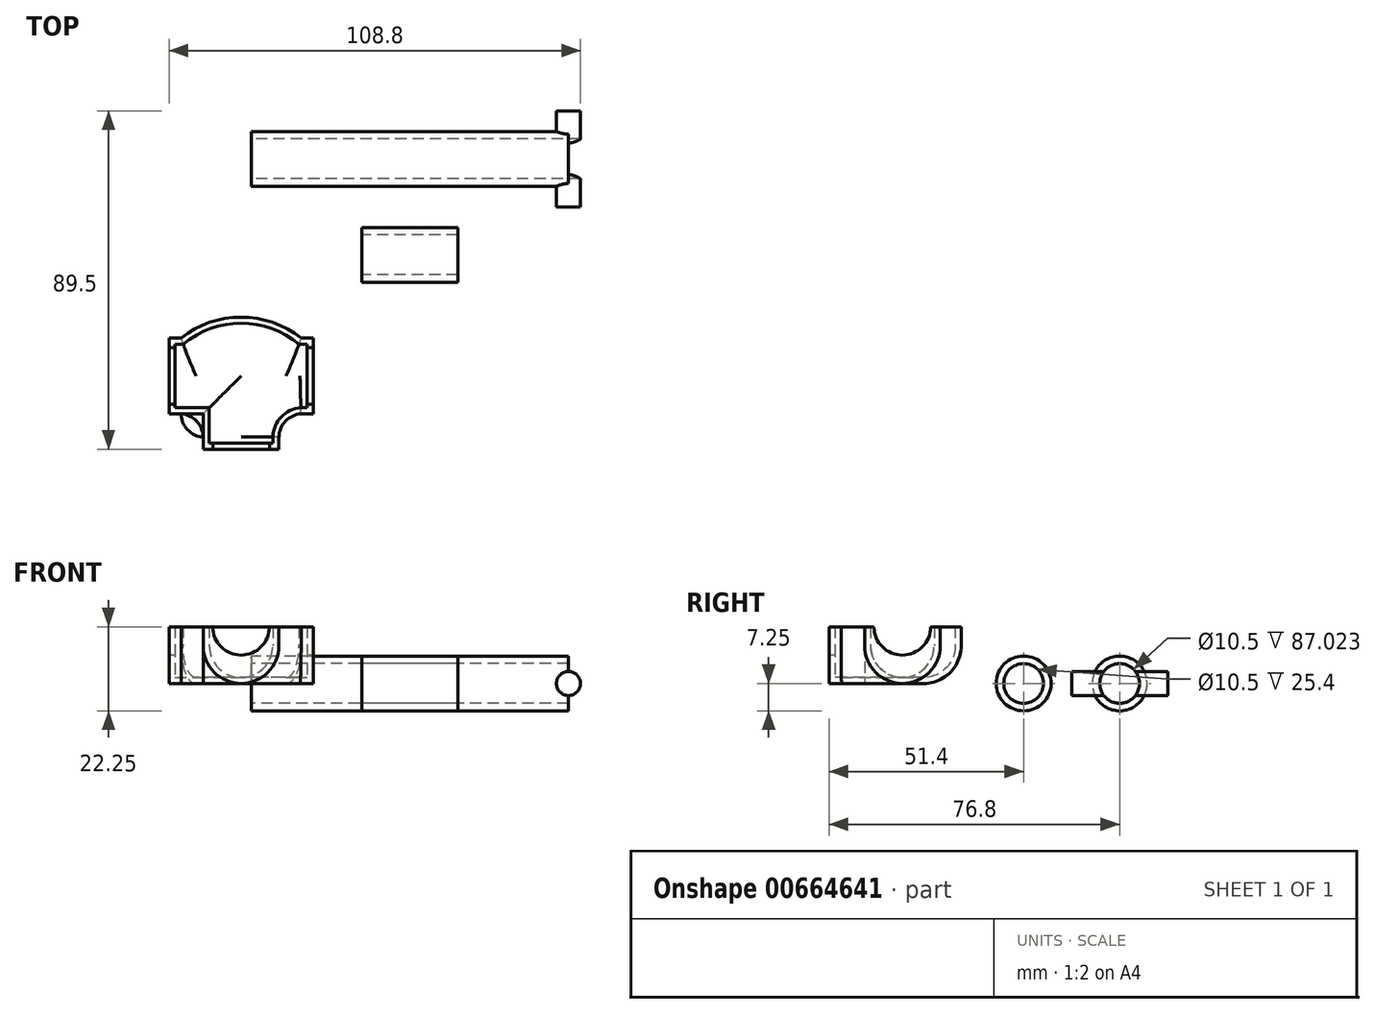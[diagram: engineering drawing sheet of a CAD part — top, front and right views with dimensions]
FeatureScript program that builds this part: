
annotation { "Feature Type Name" : "Feature", "Feature Type Description" : "" }
export const myFeature = defineFeature(function(context is Context, id is Id, definition is map)
    precondition{}
    {
        {
            var Q0;
            Q0=qCreatedBy(makeId("Right.planeOp"),FACE);
            var sketch = newSketch(context, id + "F0", { "sketchPlane" : qUnion([Q0])});
            skCircle(sketch, "E0", {"center": v(0, 0) * mm, "radius": 5.25 * mm});
            skCircle(sketch, "E1", {"center": v(0, 0) * mm, "radius": 7.25 * mm});
            skCircle(sketch, "E2.1.0.0", {"center": v(25.4, 0) * mm, "radius": 7.25 * mm});
            skCircle(sketch, "E2.1.0.1", {"center": v(25.4, 0) * mm, "radius": 5.25 * mm});
            skLineSegment(sketch, "E2.direction1", {"start": v(0, 0) * mm, "end": v(25.4, 0) * mm, "construction": true});
            skSolve(sketch);
        }
        {
            var Q0;
            Q0=makeQuery(id+"F0.imprint","IMPRINT",FACE,{"disambiguationData":[TD([[makeQuery(id+"F0.imprint","IMPRINT",EDGE,{"derivedFrom":sQuery(id+"F0.wireOp",EDGE,"E0")}),-1.0]])]});
            extrude(context, id + "F1", {"entities" : qUnion([Q0]), "endBound" : BoundingType.SYMMETRIC, "depth" : 25.4 * mm, "offsetDistance" : 25 * mm});
        }
        {
            var Q0;
            Q0=makeQuery(id+"F0.imprint","IMPRINT",FACE,{"disambiguationData":[TD([[makeQuery(id+"F0.imprint","IMPRINT",EDGE,{"derivedFrom":sQuery(id+"F0.wireOp",EDGE,"E2.1.0.0")}),1.0]])]});
            extrude(context, id + "F2", {"entities" : qUnion([Q0]), "endBound" : BoundingType.SYMMETRIC, "depth" : 83.85 * mm, "offsetDistance" : 25.4 * mm});
        }
        {
            var Q0;
            Q0=qCreatedBy(makeId("Top.planeOp"),FACE);
            var sketch = newSketch(context, id + "F3", { "sketchPlane" : qUnion([Q0])});
            skArc(sketch, "E3", {"start": v(-28.77, -22.05) * mm, "mid": v(-44.65, -16.48) * mm, "end": v(-60.52, -22.05) * mm});
            skLineSegment(sketch, "E4.bottom", {"start": v(-60.52, -22.05) * mm, "end": v(-63.7, -22.05) * mm});
            skLineSegment(sketch, "E4.top", {"start": v(-60.52, -42.05) * mm, "end": v(-63.7, -42.05) * mm});
            skLineSegment(sketch, "E4.left", {"start": v(-60.52, -22.05) * mm, "end": v(-60.52, -42.05) * mm});
            skLineSegment(sketch, "E4.right", {"start": v(-63.7, -22.05) * mm, "end": v(-63.7, -42.05) * mm});
            skLineSegment(sketch, "E5.bottom", {"start": v(-28.77, -22.05) * mm, "end": v(-25.6, -22.05) * mm});
            skLineSegment(sketch, "E5.top", {"start": v(-28.77, -42.05) * mm, "end": v(-25.6, -42.05) * mm});
            skLineSegment(sketch, "E5.left", {"start": v(-28.77, -22.05) * mm, "end": v(-28.77, -42.05) * mm});
            skLineSegment(sketch, "E5.right", {"start": v(-25.6, -22.05) * mm, "end": v(-25.6, -42.05) * mm});
            skLineSegment(sketch, "E6.bottom", {"start": v(-54.65, -48.23) * mm, "end": v(-34.65, -48.23) * mm});
            skLineSegment(sketch, "E6.top", {"start": v(-54.65, -51.4) * mm, "end": v(-34.65, -51.4) * mm});
            skLineSegment(sketch, "E6.left", {"start": v(-54.65, -48.23) * mm, "end": v(-54.65, -51.4) * mm});
            skLineSegment(sketch, "E6.right", {"start": v(-34.65, -48.23) * mm, "end": v(-34.65, -51.4) * mm});
            skArc(sketch, "E7", {"start": v(-54.65, -48.23) * mm, "mid": v(-58.78, -46.27) * mm, "end": v(-60.52, -42.05) * mm});
            skArc(sketch, "E8", {"start": v(-28.77, -42.05) * mm, "mid": v(-32.9, -44) * mm, "end": v(-34.65, -48.23) * mm});
            skLineSegment(sketch, "E9", {"start": v(-44.65, -16.48) * mm, "end": v(-44.65, -48.23) * mm});
            skArc(sketch, "E10.MirrorCS", {"start": v(-60.52, -42.05) * mm, "mid": v(-56.4, -44) * mm, "end": v(-54.65, -48.23) * mm});
            skArc(sketch, "E11.MirrorCS", {"start": v(-34.65, -48.23) * mm, "mid": v(-30.52, -46.27) * mm, "end": v(-28.77, -42.05) * mm});
            skLineSegment(sketch, "E12.bottom", {"start": v(-60.52, -22.05) * mm, "end": v(-28.77, -22.05) * mm});
            skLineSegment(sketch, "E12.top", {"start": v(-60.52, -12.53) * mm, "end": v(-28.77, -12.53) * mm});
            skLineSegment(sketch, "E12.left", {"start": v(-60.52, -22.05) * mm, "end": v(-60.52, -12.53) * mm});
            skLineSegment(sketch, "E12.right", {"start": v(-28.77, -22.05) * mm, "end": v(-28.77, -12.53) * mm});
            skArc(sketch, "E13", {"start": v(-57.35, -12.53) * mm, "mid": v(-59.6, -13.46) * mm, "end": v(-60.52, -15.7) * mm});
            skArc(sketch, "E14.MirrorCS", {"start": v(-31.95, -12.53) * mm, "mid": v(-29.7, -13.46) * mm, "end": v(-28.77, -15.7) * mm});
            skLineSegment(sketch, "E15.bottom", {"start": v(-60.52, -42.05) * mm, "end": v(-54.65, -42.05) * mm});
            skLineSegment(sketch, "E15.top", {"start": v(-60.52, -48.23) * mm, "end": v(-54.65, -48.23) * mm});
            skLineSegment(sketch, "E15.left", {"start": v(-60.52, -42.05) * mm, "end": v(-60.52, -48.23) * mm});
            skLineSegment(sketch, "E15.right", {"start": v(-54.65, -42.05) * mm, "end": v(-54.65, -48.23) * mm});
            skLineSegment(sketch, "E16.bottom", {"start": v(-28.77, -42.05) * mm, "end": v(-34.65, -42.05) * mm});
            skLineSegment(sketch, "E16.top", {"start": v(-28.77, -48.23) * mm, "end": v(-34.65, -48.23) * mm});
            skLineSegment(sketch, "E16.left", {"start": v(-28.77, -48.23) * mm, "end": v(-28.77, -42.05) * mm});
            skLineSegment(sketch, "E16.right", {"start": v(-34.65, -48.23) * mm, "end": v(-34.65, -42.05) * mm});
            skSolve(sketch);
        }
        {
            var Q0;
            {var subQ3=sQuery(id+"F3.wireOp",EDGE,"E5.left");Q0=makeQuery(id+"F3.imprint","IMPRINT",FACE,{"disambiguationData":[TD([[makeQuery(id+"F3.imprint","IMPRINT",EDGE,{"derivedFrom":subQ3}),-1.0]])]});}
            var Q1;
            {var subQ3=sQuery(id+"F3.wireOp",EDGE,"E4.left");Q1=makeQuery(id+"F3.imprint","IMPRINT",FACE,{"disambiguationData":[TD([[makeQuery(id+"F3.imprint","IMPRINT",EDGE,{"derivedFrom":subQ3}),1.0]])]});}
            var Q2;
            Q2=makeQuery(id+"F3.imprint","IMPRINT",FACE,{"disambiguationData":[TD([[makeQuery(id+"F3.imprint","IMPRINT",EDGE,{"derivedFrom":sQuery(id+"F3.wireOp",EDGE,"E4.bottom")}),1.0]])]});
            var Q3;
            Q3=makeQuery(id+"F3.imprint","IMPRINT",FACE,{"disambiguationData":[TD([[makeQuery(id+"F3.imprint","IMPRINT",EDGE,{"derivedFrom":sQuery(id+"F3.wireOp",EDGE,"E6.top")}),1.0]])]});
            var Q4;
            Q4=makeQuery(id+"F3.imprint","IMPRINT",FACE,{"disambiguationData":[TD([[makeQuery(id+"F3.imprint","IMPRINT",EDGE,{"derivedFrom":sQuery(id+"F3.wireOp",EDGE,"E5.bottom")}),-1.0]])]});
            var Q5;
            {var subQ0=sQuery(id+"F3.wireOp",EDGE,"E16.bottom");var subQ1=sQuery(id+"F3.wireOp",EDGE,"E8");var subQ2=makeQuery(id+"F3.imprint","INTERSECT",VERTEX,{"derivedFrom":[subQ1,subQ0]});Q5=makeQuery(id+"F3.imprint","IMPRINT",FACE,{"disambiguationData":[TD([[makeQuery(id+"F3.imprint","IMPRINT",EDGE,{"disambiguationData":[TD([[subQ2,-1.0]])],"derivedFrom":subQ1}),-1.0]])]});}
            var Q6;
            {var subQ1=sQuery(id+"F3.wireOp",EDGE,"E3");var subQ3=sQuery(id+"F3.wireOp",EDGE,"E9");var subQ4=makeQuery(id+"F3.imprint","INTERSECT",VERTEX,{"derivedFrom":[subQ1,subQ3]});Q6=makeQuery(id+"F3.imprint","IMPRINT",FACE,{"disambiguationData":[TD([[makeQuery(id+"F3.imprint","IMPRINT",EDGE,{"disambiguationData":[TD([[subQ4,-1.0]])],"derivedFrom":subQ3}),-1.0]])]});}
            var Q7;
            {var subQ1=sQuery(id+"F3.wireOp",EDGE,"E3");var subQ3=sQuery(id+"F3.wireOp",EDGE,"E9");var subQ4=makeQuery(id+"F3.imprint","INTERSECT",VERTEX,{"derivedFrom":[subQ1,subQ3]});Q7=makeQuery(id+"F3.imprint","IMPRINT",FACE,{"disambiguationData":[TD([[makeQuery(id+"F3.imprint","IMPRINT",EDGE,{"disambiguationData":[TD([[subQ4,-1.0]])],"derivedFrom":subQ3}),1.0]])]});}
            var Q8;
            {var subQ0=sQuery(id+"F3.wireOp",EDGE,"E15.bottom");var subQ1=sQuery(id+"F3.wireOp",EDGE,"E10.MirrorCS");var subQ2=makeQuery(id+"F3.imprint","INTERSECT",VERTEX,{"derivedFrom":[subQ1,subQ0]});Q8=makeQuery(id+"F3.imprint","IMPRINT",FACE,{"disambiguationData":[TD([[makeQuery(id+"F3.imprint","IMPRINT",EDGE,{"disambiguationData":[TD([[subQ2,-1.0]])],"derivedFrom":subQ1}),1.0]])]});}
            extrude(context, id + "F4", {"entities" : qUnion([Q0, Q1, Q2, Q3, Q4, Q5, Q6, Q7, Q8]), "depth" : 15 * mm, "offsetDistance" : 25.4 * mm});
        }
        {
            var Q0;
            Q0=makeQuery(id+"F4.opExtrude","CAP_EDGE",EDGE,{"disambiguationData":[OSD([sQuery(id+"F3.wireOp",EDGE,"E4.top")])],"isStart":true});
            var Q1;
            Q1=makeQuery(id+"F4.opExtrude","CAP_EDGE",EDGE,{"disambiguationData":[OSD([sQuery(id+"F3.wireOp",EDGE,"E7")])],"isStart":true});
            var Q2;
            Q2=makeQuery(id+"F4.opExtrude","CAP_EDGE",EDGE,{"disambiguationData":[OSD([sQuery(id+"F3.wireOp",EDGE,"E6.left")])],"isStart":true});
            var Q3;
            Q3=makeQuery(id+"F4.opExtrude","CAP_EDGE",EDGE,{"disambiguationData":[OSD([sQuery(id+"F3.wireOp",EDGE,"E5.top")])],"isStart":true});
            var Q4;
            Q4=makeQuery(id+"F4.opExtrude","CAP_EDGE",EDGE,{"disambiguationData":[OSD([sQuery(id+"F3.wireOp",EDGE,"E6.right")])],"isStart":true});
            var Q5;
            Q5=makeQuery(id+"F4.opExtrude","CAP_EDGE",EDGE,{"disambiguationData":[OSD([sQuery(id+"F3.wireOp",EDGE,"E8")])],"isStart":true});
            var Q6;
            Q6=makeQuery(id+"F4.opExtrude","CAP_EDGE",EDGE,{"disambiguationData":[OSD([sQuery(id+"F3.wireOp",EDGE,"E3")])],"isStart":true});
            var Q7;
            Q7=makeQuery(id+"F4.opExtrude","CAP_EDGE",EDGE,{"disambiguationData":[OSD([sQuery(id+"F3.wireOp",EDGE,"E10.MirrorCS")])],"isStart":true});
            var Q8;
            Q8=makeQuery(id+"F4.opExtrude","CAP_EDGE",EDGE,{"disambiguationData":[OSD([sQuery(id+"F3.wireOp",EDGE,"E4.bottom")])],"isStart":true});
            var Q9;
            Q9=makeQuery(id+"F4.opExtrude","CAP_EDGE",EDGE,{"disambiguationData":[OSD([sQuery(id+"F3.wireOp",EDGE,"E5.bottom")])],"isStart":true});
            fillet(context, id + "F5", {"entities" : qUnion([Q0, Q1, Q2, Q3, Q4, Q5, Q6, Q7, Q8, Q9]), "radius" : 10 * mm, "tangentPropagation" : true, "allowEdgeOverflow" : false});
        }
        {
            var Q0;
            Q0=makeQuery(id+"F4.opExtrude","CAP_FACE",FACE,{"disambiguationData":[OSD([sQuery(id+"F3.wireOp",EDGE,"E3"),sQuery(id+"F3.wireOp",EDGE,"E4.bottom"),sQuery(id+"F3.wireOp",EDGE,"E4.top"),sQuery(id+"F3.wireOp",EDGE,"E4.right"),sQuery(id+"F3.wireOp",EDGE,"E5.bottom"),sQuery(id+"F3.wireOp",EDGE,"E5.top"),sQuery(id+"F3.wireOp",EDGE,"E5.right"),sQuery(id+"F3.wireOp",EDGE,"E6.top"),sQuery(id+"F3.wireOp",EDGE,"E6.left"),sQuery(id+"F3.wireOp",EDGE,"E6.right"),sQuery(id+"F3.wireOp",EDGE,"E7"),sQuery(id+"F3.wireOp",EDGE,"E8")])],"isStart":false});
            shell(context, id + "F6", {"entities" : qUnion([Q0]), "thickness" : 1.59 * mm});
        }
        {
            var Q0;
            Q0=makeQuery(id+"F4.opExtrude","SWEPT_FACE",FACE,{"disambiguationData":[OSD([sQuery(id+"F3.wireOp",EDGE,"E4.right")])]});
            var sketch = newSketch(context, id + "F7", { "sketchPlane" : qUnion([Q0])});
            skCircle(sketch, "E17", {"center": v(32.05, 15) * mm, "radius": 7.5 * mm});
            skSolve(sketch);
        }
        {
            var Q0;
            Q0 = qSketchRegion(id + "F7", true);
            extrude(context, id + "F8", {"entities" : qUnion([Q0]), "operationType" : NewBodyOperationType.REMOVE, "endBound" : BoundingType.THROUGH_ALL, "oppositeDirection" : true, "depth" : 25.4 * mm, "offsetDistance" : 25.4 * mm});
        }
        {
            var Q0;
            Q0=makeQuery(id+"F4.opExtrude","SWEPT_FACE",FACE,{"disambiguationData":[OSD([sQuery(id+"F3.wireOp",EDGE,"E6.top")])]});
            var sketch = newSketch(context, id + "F9", { "sketchPlane" : qUnion([Q0])});
            skCircle(sketch, "E18", {"center": v(-44.65, 15) * mm, "radius": 7.5 * mm});
            skSolve(sketch);
        }
        {
            var Q0;
            {var subQ0=sQuery(id+"F9.wireOp",EDGE,"E18");var subQ1=makeQuery(id+"F4.opExtrude","CAP_EDGE",EDGE,{"disambiguationData":[OSD([sQuery(id+"F3.wireOp",EDGE,"E6.top")])],"isStart":false});var subQ2=makeQuery(id+"F9.imprint","INTERSECT",VERTEX,{"disambiguationData":[OD(0.0)],"derivedFrom":[subQ1,subQ0]});Q0=makeQuery(id+"F9.imprint","IMPRINT",FACE,{"disambiguationData":[TD([[makeQuery(id+"F9.imprint","IMPRINT",EDGE,{"disambiguationData":[TD([[subQ2,-1.0]])],"derivedFrom":subQ0}),1.0]])]});}
            extrude(context, id + "F10", {"entities" : qUnion([Q0]), "operationType" : NewBodyOperationType.REMOVE, "oppositeDirection" : true, "depth" : 12.7 * mm, "offsetDistance" : 25.4 * mm});
        }
        {
            var Q0;
            Q0=qCreatedBy(makeId("Front.planeOp"),FACE);
            cPlane(context, id + "F11", {"entities" : qUnion([Q0]), "cplaneType" : CPlaneType.OFFSET, "offset" : 25.4 * mm, "oppositeDirection" : true, "width" : 152.4 * mm, "height" : 152.4 * mm});
        }
        {
            var Q0;
            Q0=qCreatedBy(id+"F11.planeOp",FACE);
            var sketch = newSketch(context, id + "F12", { "sketchPlane" : qUnion([Q0])});
            skCircle(sketch, "E19", {"center": v(41.92, 0) * mm, "radius": 3.18 * mm});
            skCircle(sketch, "E20", {"center": v(41.92, 0) * mm, "radius": 7.25 * mm});
            skSolve(sketch);
        }
        {
            var Q0;
            Q0=makeQuery(id+"F12.imprint","IMPRINT",FACE,{"disambiguationData":[TD([[makeQuery(id+"F12.imprint","IMPRINT",EDGE,{"derivedFrom":sQuery(id+"F12.wireOp",EDGE,"E19")}),1.0]])]});
            extrude(context, id + "F13", {"entities" : qUnion([Q0]), "operationType" : NewBodyOperationType.ADD, "endBound" : BoundingType.SYMMETRIC, "depth" : 25.4 * mm, "offsetDistance" : 25.4 * mm});
        }
        {
            var Q0;
            Q0=makeQuery(id+"F0.imprint","IMPRINT",FACE,{"disambiguationData":[TD([[makeQuery(id+"F0.imprint","IMPRINT",EDGE,{"derivedFrom":sQuery(id+"F0.wireOp",EDGE,"E2.1.0.1")}),1.0]])]});
            extrude(context, id + "F14", {"entities" : qUnion([Q0]), "operationType" : NewBodyOperationType.REMOVE, "depth" : 101.6 * mm, "offsetDistance" : 25.4 * mm});
        }
    });
